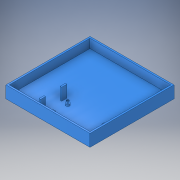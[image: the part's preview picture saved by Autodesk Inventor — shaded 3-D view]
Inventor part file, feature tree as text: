
AUTODESK INVENTOR PART (.ipt)
format: ipt  version: 2019.3 (Build 233278000, 278)  size: 221,696 bytes
history: native  units: in
note: dims shown in document units (in); Inventor stores cm internally (conversion verified against a paired STEP export)
features: sketch x7, extrude x4, hole x4
ambient origin geometry x8: Origin, YZ Plane, XZ Plane, XY Plane, X Axis, Y Axis, Z Axis, Center Point
bodies: Solid1 (feature_tree)
feature tree (15):
  extrude  "Extrusion1"  Depth=1.6717in
  extrude  "Extrusion3"  Depth=0.2in
  hole  "Hole9"  [1 undecoded]
  hole  "Hole13"  [1 undecoded]
  hole  "Hole16"  [1 undecoded]
  extrude  "Extrusion12"  Depth=0.1in
  extrude  "Extrusion13"  Depth=0.1in
  sketch  "Sketch1"  dims[d0=3.0496in d1=1.6717in]
  sketch  "Sketch3"  dims[d2=0.2in d3=0.0in d8=0.9055in]
  sketch  "Sketch22"  dims[d9=2.2835in d17=0.7874in d19=2.2835in]
  hole  "Hole12"  [1 undecoded]
  sketch  "Sketch23"  dims[d20=0.7874in d22=0.9055in d25=0.2362in]
  sketch  "Sketch25"  dims[d26=0.1in d27=0.0in]
  sketch  "Sketch26"  dims[d138=0.1495in d139=0.75in d140=0.375in d141=0.25in d142=0.5635in d143=1.0in d144=0.0in]
  sketch  "Sketch27"  dims[d145=0.191in d146=0.75in d147=0.375in d148=0.25in d149=0.5635in d150=0.15in d151=0.0in d166=0.096in d167=0.75in d168=0.1285in d169=0.157in d170=0.5635in d171=1.0in d172=0.8108in d175=0.1in d176=0.1in d177=0.1in d178=0.1in d180=0.0in d181=3.05in d182=0.1in d183=0.3in d184=0.15in d185=1.62in d186=1.0in d187=0.75in d188=0.0in]
note: 4 required parameter values undecoded (feature->parameter linkage not recoverable at this tier; creation-order binding heuristic only, values carry confidence <= 0.55)
